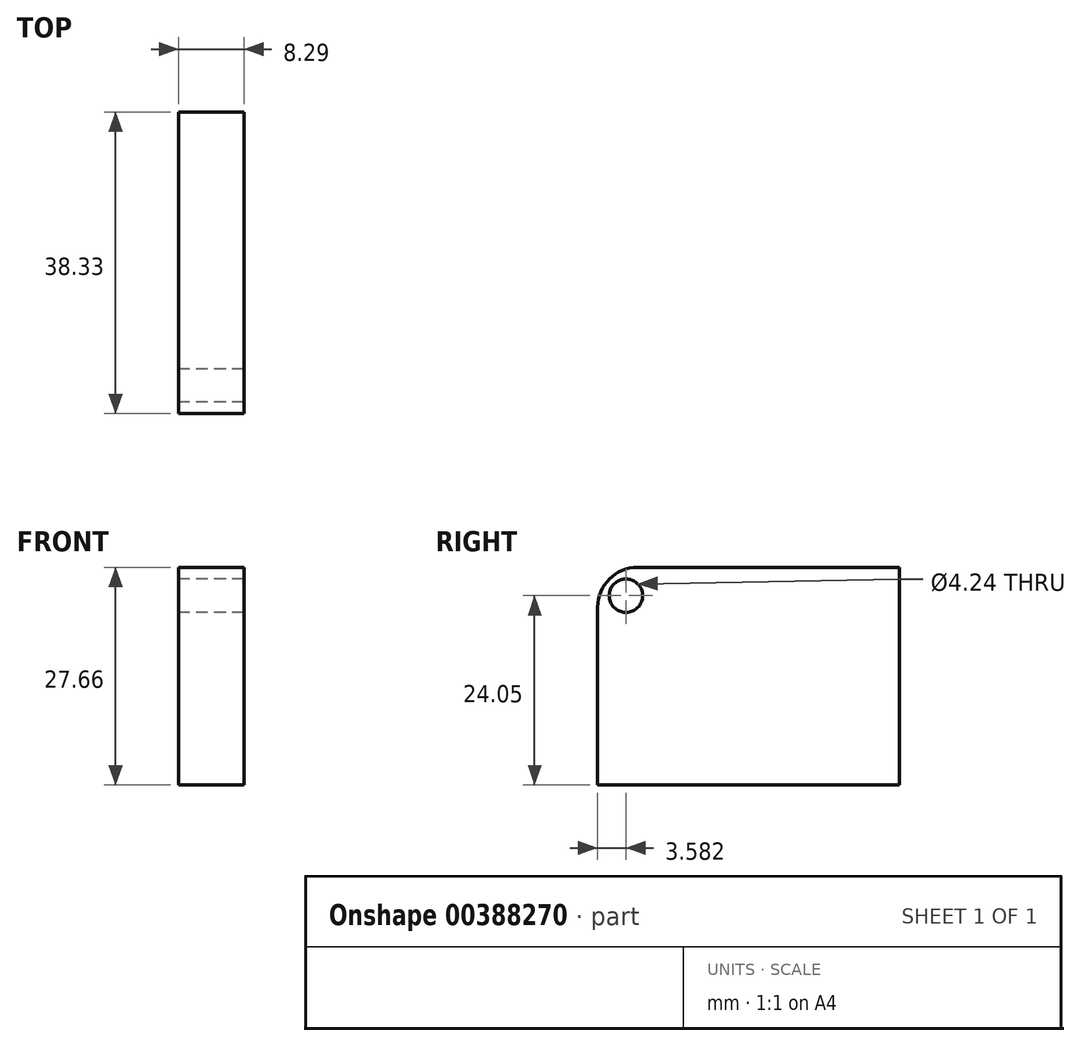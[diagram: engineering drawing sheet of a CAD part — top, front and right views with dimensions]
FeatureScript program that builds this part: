
annotation { "Feature Type Name" : "Feature", "Feature Type Description" : "" }
export const myFeature = defineFeature(function(context is Context, id is Id, definition is map)
    precondition{}
    {
        {
            var Q0;
            Q0=qCreatedBy(makeId("Top.planeOp"),FACE);
            var sketch = newSketch(context, id + "F0", { "sketchPlane" : qUnion([Q0])});
            skLineSegment(sketch, "E0.bottom", {"start": v(-47.3, 13.9) * mm, "end": v(-55.6, 13.9) * mm});
            skLineSegment(sketch, "E0.top", {"start": v(-47.3, -24.44) * mm, "end": v(-55.6, -24.44) * mm});
            skLineSegment(sketch, "E0.left", {"start": v(-47.3, 13.9) * mm, "end": v(-47.3, -24.44) * mm});
            skLineSegment(sketch, "E0.right", {"start": v(-55.6, 13.9) * mm, "end": v(-55.6, -24.44) * mm});
            skSolve(sketch);
        }
        {
            var Q0;
            Q0 = qSketchRegion(id + "F0", true);
            extrude(context, id + "F1", {"entities" : qUnion([Q0]), "depth" : 27.66 * mm});
        }
        {
            var Q0;
            Q0=makeQuery(id+"F1.opExtrude","CAP_EDGE",EDGE,{"disambiguationData":[OSD([sQuery(id+"F0.wireOp",EDGE,"E0.top")])],"isStart":false});
            fillet(context, id + "F2", {"entities" : qUnion([Q0]), "radius" : 5.08 * mm, "tangentPropagation" : true, "allowEdgeOverflow" : false});
        }
        {
            var Q0;
            Q0=makeQuery(id+"F1.opExtrude","SWEPT_FACE",FACE,{"disambiguationData":[OSD([sQuery(id+"F0.wireOp",EDGE,"E0.right")])]});
            var sketch = newSketch(context, id + "F3", { "sketchPlane" : qUnion([Q0])});
            skCircle(sketch, "E1", {"center": v(20.86, 24.05) * mm, "radius": 2.12 * mm});
            skSolve(sketch);
        }
        {
            var Q0;
            Q0 = qSketchRegion(id + "F3", true);
            extrude(context, id + "F4", {"entities" : qUnion([Q0]), "operationType" : NewBodyOperationType.REMOVE, "oppositeDirection" : true, "depth" : 25.4 * mm});
        }
    });
